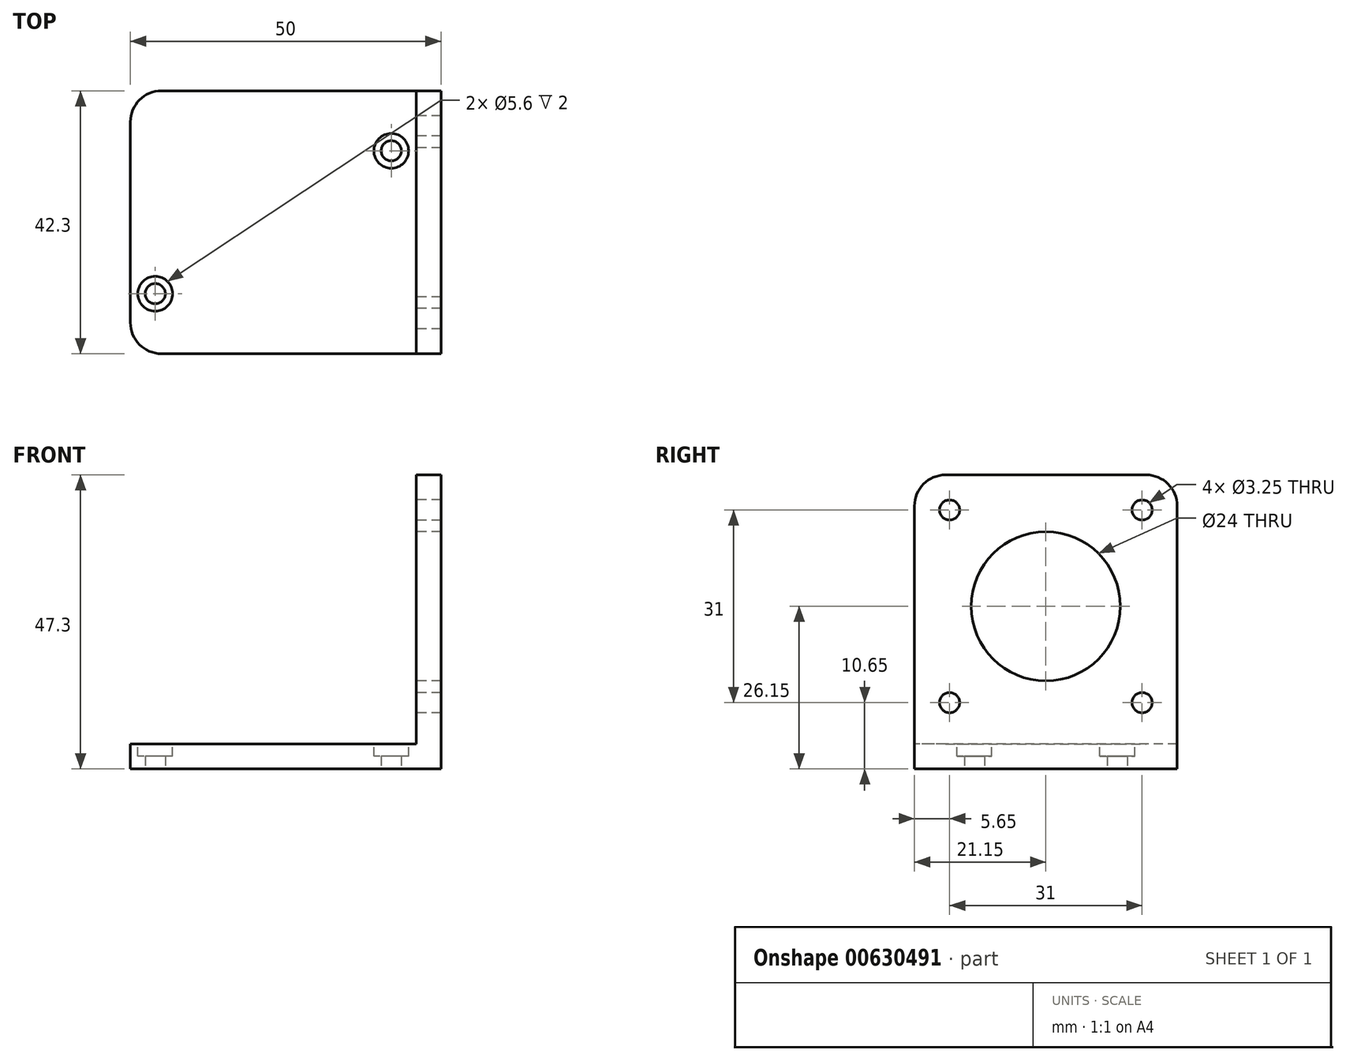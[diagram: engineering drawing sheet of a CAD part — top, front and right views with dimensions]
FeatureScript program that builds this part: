
annotation { "Feature Type Name" : "Feature", "Feature Type Description" : "" }
export const myFeature = defineFeature(function(context is Context, id is Id, definition is map)
    precondition{}
    {
        {
            var Q0;
            Q0=qCreatedBy(makeId("Top.planeOp"),FACE);
            var sketch = newSketch(context, id + "F0", { "sketchPlane" : qUnion([Q0])});
            skLineSegment(sketch, "E0.bottom", {"start": v(0, 0) * mm, "end": v(50, 0) * mm});
            skLineSegment(sketch, "E0.top", {"start": v(0, 42.3) * mm, "end": v(50, 42.3) * mm});
            skLineSegment(sketch, "E0.left", {"start": v(0, 0) * mm, "end": v(0, 42.3) * mm});
            skLineSegment(sketch, "E0.right", {"start": v(50, 0) * mm, "end": v(50, 42.3) * mm});
            skCircle(sketch, "E1", {"center": v(4, 9.65) * mm, "radius": 1.63 * mm});
            skCircle(sketch, "E2", {"center": v(4, 9.65) * mm, "radius": 2.8 * mm});
            skCircle(sketch, "E3", {"center": v(42, 32.65) * mm, "radius": 1.63 * mm});
            skCircle(sketch, "E4", {"center": v(42, 32.65) * mm, "radius": 2.8 * mm});
            skSolve(sketch);
        }
        {
            var Q0;
            Q0=makeQuery(id+"F0.imprint","IMPRINT",FACE,{"disambiguationData":[TD([[makeQuery(id+"F0.imprint","IMPRINT",EDGE,{"derivedFrom":sQuery(id+"F0.wireOp",EDGE,"E0.bottom")}),1.0]])]});
            var Q1;
            Q1=makeQuery(id+"F0.imprint","IMPRINT",FACE,{"disambiguationData":[TD([[makeQuery(id+"F0.imprint","IMPRINT",EDGE,{"derivedFrom":sQuery(id+"F0.wireOp",EDGE,"E3")}),-1.0]])]});
            var Q2;
            Q2=makeQuery(id+"F0.imprint","IMPRINT",FACE,{"disambiguationData":[TD([[makeQuery(id+"F0.imprint","IMPRINT",EDGE,{"derivedFrom":sQuery(id+"F0.wireOp",EDGE,"E1")}),-1.0]])]});
            extrude(context, id + "F1", {"entities" : qUnion([Q0, Q1, Q2]), "depth" : 4 * mm, "offsetDistance" : 25 * mm});
        }
        {
            var Q0;
            Q0=makeQuery(id+"F1.opExtrude","CAP_FACE",FACE,{"disambiguationData":[OSD([sQuery(id+"F0.wireOp",EDGE,"E0.bottom"),sQuery(id+"F0.wireOp",EDGE,"E0.top"),sQuery(id+"F0.wireOp",EDGE,"E0.left"),sQuery(id+"F0.wireOp",EDGE,"E0.right"),sQuery(id+"F0.wireOp",EDGE,"E1"),sQuery(id+"F0.wireOp",EDGE,"E3")])],"isStart":false});
            var sketch = newSketch(context, id + "F2", { "sketchPlane" : qUnion([Q0])});
            skCircle(sketch, "E5", {"center": v(4, 9.65) * mm, "radius": 2.8 * mm});
            skCircle(sketch, "E6", {"center": v(42, 32.65) * mm, "radius": 2.8 * mm});
            skSolve(sketch);
        }
        {
            var Q0;
            Q0=makeQuery(id+"F2.imprint","IMPRINT",FACE,{"disambiguationData":[TD([[makeQuery(id+"F2.imprint","IMPRINT",EDGE,{"derivedFrom":sQuery(id+"F2.wireOp",EDGE,"E5")}),1.0]])]});
            var Q1;
            Q1=makeQuery(id+"F2.imprint","IMPRINT",FACE,{"disambiguationData":[TD([[makeQuery(id+"F2.imprint","IMPRINT",EDGE,{"derivedFrom":sQuery(id+"F2.wireOp",EDGE,"E6")}),1.0]])]});
            extrude(context, id + "F3", {"entities" : qUnion([Q0, Q1]), "operationType" : NewBodyOperationType.REMOVE, "oppositeDirection" : true, "depth" : 2 * mm, "offsetDistance" : 25 * mm});
        }
        {
            var Q0;
            Q0=makeQuery(id+"F1.opExtrude","CAP_FACE",FACE,{"disambiguationData":[OSD([sQuery(id+"F0.wireOp",EDGE,"E0.bottom"),sQuery(id+"F0.wireOp",EDGE,"E0.top"),sQuery(id+"F0.wireOp",EDGE,"E0.left"),sQuery(id+"F0.wireOp",EDGE,"E0.right"),sQuery(id+"F0.wireOp",EDGE,"E1"),sQuery(id+"F0.wireOp",EDGE,"E3")])],"isStart":false});
            var sketch = newSketch(context, id + "F4", { "sketchPlane" : qUnion([Q0])});
            skLineSegment(sketch, "E7", {"start": v(46, 42.3) * mm, "end": v(46, 0) * mm});
            skSolve(sketch);
        }
        {
            var Q0;
            {var subQ0=sQuery(id+"F4.wireOp",EDGE,"E7");Q0=makeQuery(id+"F4.imprint","IMPRINT",FACE,{"disambiguationData":[TD([[makeQuery(id+"F4.imprint","IMPRINT",EDGE,{"derivedFrom":subQ0}),1.0]])]});}
            extrude(context, id + "F5", {"entities" : qUnion([Q0]), "operationType" : NewBodyOperationType.ADD, "depth" : 43.3 * mm, "offsetDistance" : 25 * mm});
        }
        {
            var Q0;
            Q0=makeQuery(id+"F5.opExtrude","SWEPT_FACE",FACE,{"disambiguationData":[OSD([sQuery(id+"F4.wireOp",EDGE,"E7")])]});
            var sketch = newSketch(context, id + "F6", { "sketchPlane" : qUnion([Q0])});
            skCircle(sketch, "E8", {"center": v(-36.65, 41.65) * mm, "radius": 1.63 * mm});
            skCircle(sketch, "E9", {"center": v(-36.65, 10.65) * mm, "radius": 1.62 * mm});
            skCircle(sketch, "E10", {"center": v(-5.65, 41.65) * mm, "radius": 1.63 * mm});
            skCircle(sketch, "E11", {"center": v(-5.65, 10.65) * mm, "radius": 1.63 * mm});
            skCircle(sketch, "E12", {"center": v(-21.15, 26.15) * mm, "radius": 12 * mm});
            skSolve(sketch);
        }
        {
            var Q0;
            Q0=makeQuery(id+"F6.imprint","IMPRINT",FACE,{"disambiguationData":[TD([[makeQuery(id+"F6.imprint","IMPRINT",EDGE,{"derivedFrom":sQuery(id+"F6.wireOp",EDGE,"E12")}),1.0]])]});
            var Q1;
            Q1=makeQuery(id+"F6.imprint","IMPRINT",FACE,{"disambiguationData":[TD([[makeQuery(id+"F6.imprint","IMPRINT",EDGE,{"derivedFrom":sQuery(id+"F6.wireOp",EDGE,"E8")}),1.0]])]});
            var Q2;
            Q2=makeQuery(id+"F6.imprint","IMPRINT",FACE,{"disambiguationData":[TD([[makeQuery(id+"F6.imprint","IMPRINT",EDGE,{"derivedFrom":sQuery(id+"F6.wireOp",EDGE,"E10")}),1.0]])]});
            var Q3;
            Q3=makeQuery(id+"F6.imprint","IMPRINT",FACE,{"disambiguationData":[TD([[makeQuery(id+"F6.imprint","IMPRINT",EDGE,{"derivedFrom":sQuery(id+"F6.wireOp",EDGE,"E11")}),1.0]])]});
            var Q4;
            Q4=makeQuery(id+"F6.imprint","IMPRINT",FACE,{"disambiguationData":[TD([[makeQuery(id+"F6.imprint","IMPRINT",EDGE,{"derivedFrom":sQuery(id+"F6.wireOp",EDGE,"E9")}),1.0]])]});
            extrude(context, id + "F7", {"entities" : qUnion([Q0, Q1, Q2, Q3, Q4]), "operationType" : NewBodyOperationType.REMOVE, "oppositeDirection" : true, "depth" : 25 * mm, "offsetDistance" : 25 * mm});
        }
        {
            var Q0;
            Q0=makeQuery(id+"F1.opExtrude","SWEPT_EDGE",EDGE,{"disambiguationData":[OSD([sQuery(id+"F0.wireOp",EDGE,"E0.bottom"),sQuery(id+"F0.wireOp",EDGE,"E0.left")])]});
            var Q1;
            Q1=makeQuery(id+"F1.opExtrude","SWEPT_EDGE",EDGE,{"disambiguationData":[OSD([sQuery(id+"F0.wireOp",EDGE,"E0.top"),sQuery(id+"F0.wireOp",EDGE,"E0.left")])]});
            var Q2;
            Q2=makeQuery(id+"F5.opExtrude","CAP_EDGE",EDGE,{"disambiguationData":[OSD([sQuery(id+"F0.wireOp",EDGE,"E0.top")])],"isStart":false});
            var Q3;
            Q3=makeQuery(id+"F5.opExtrude","CAP_EDGE",EDGE,{"disambiguationData":[OSD([sQuery(id+"F0.wireOp",EDGE,"E0.bottom")])],"isStart":false});
            fillet(context, id + "F8", {"entities" : qUnion([Q0, Q1, Q2, Q3]), "radius" : 5 * mm, "tangentPropagation" : true, "allowEdgeOverflow" : false});
        }
    });
